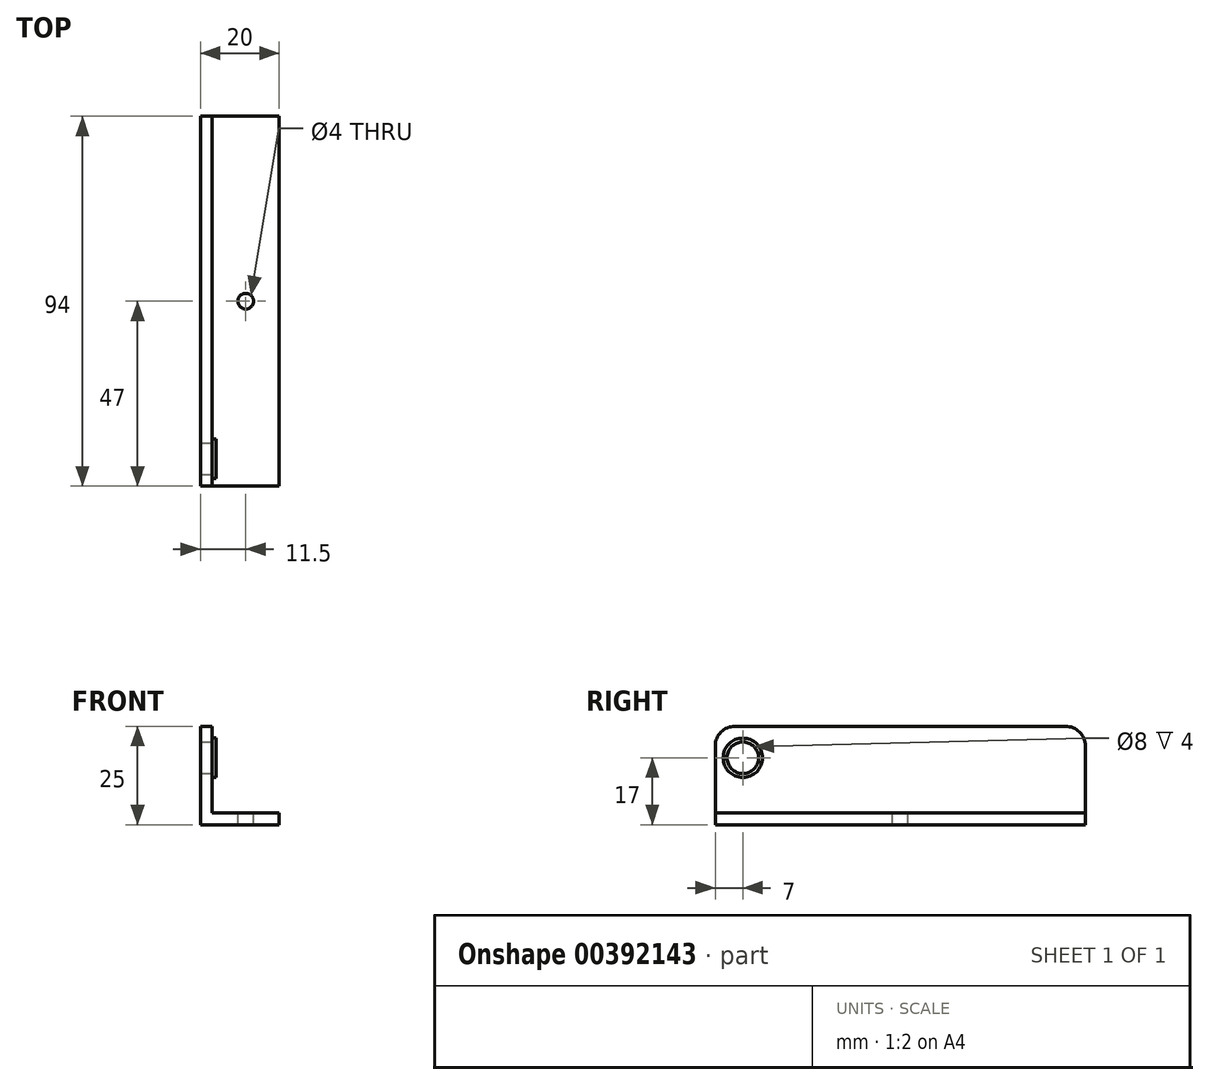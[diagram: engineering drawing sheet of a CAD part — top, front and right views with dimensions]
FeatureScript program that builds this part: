
annotation { "Feature Type Name" : "Feature", "Feature Type Description" : "" }
export const myFeature = defineFeature(function(context is Context, id is Id, definition is map)
    precondition{}
    {
        {
            var Q0;
            Q0=qCreatedBy(makeId("Top.planeOp"),FACE);
            var sketch = newSketch(context, id + "F0", { "sketchPlane" : qUnion([Q0])});
            skLineSegment(sketch, "E0.bottom", {"start": v(-65, 47) * mm, "end": v(-45, 47) * mm});
            skLineSegment(sketch, "E0.top", {"start": v(-65, -47) * mm, "end": v(-45, -47) * mm});
            skLineSegment(sketch, "E0.left", {"start": v(-65, 47) * mm, "end": v(-65, -47) * mm});
            skLineSegment(sketch, "E0.right", {"start": v(-45, 47) * mm, "end": v(-45, -47) * mm});
            skLineSegment(sketch, "E1", {"start": v(0, 47) * mm, "end": v(0, -47) * mm, "construction": true});
            skSolve(sketch);
        }
        {
            var Q0;
            Q0=makeQuery(id+"F0.imprint","IMPRINT",FACE,{"disambiguationData":[TD([[makeQuery(id+"F0.imprint","IMPRINT",EDGE,{"derivedFrom":sQuery(id+"F0.wireOp",EDGE,"E0.bottom")}),-1.0]])]});
            extrude(context, id + "F1", {"entities" : qUnion([Q0]), "depth" : 25 * mm});
        }
        {
            var Q0;
            Q0=makeQuery(id+"F1.opExtrude","SWEPT_FACE",FACE,{"disambiguationData":[OSD([sQuery(id+"F0.wireOp",EDGE,"E0.right")])]});
            var sketch = newSketch(context, id + "F2", { "sketchPlane" : qUnion([Q0])});
            skLineSegment(sketch, "E2.bottom", {"start": v(-47, 25) * mm, "end": v(47, 25) * mm});
            skLineSegment(sketch, "E2.top", {"start": v(-47, 3) * mm, "end": v(47, 3) * mm});
            skLineSegment(sketch, "E2.left", {"start": v(-47, 25) * mm, "end": v(-47, 3) * mm});
            skLineSegment(sketch, "E2.right", {"start": v(47, 25) * mm, "end": v(47, 3) * mm});
            skLineSegment(sketch, "E3", {"start": v(0, 0) * mm, "end": v(0, 25) * mm, "construction": true});
            skCircle(sketch, "E4", {"center": v(-40, 17) * mm, "radius": 11 * mm});
            skCircle(sketch, "E5", {"center": v(-40, 17) * mm, "radius": 13 * mm});
            skCircle(sketch, "E6", {"center": v(-40, 17) * mm, "radius": 4 * mm});
            skCircle(sketch, "E7", {"center": v(-40, 17) * mm, "radius": 5 * mm});
            skSolve(sketch);
        }
        {
            var Q0;
            {var subQ1=sQuery(id+"F2.wireOp",EDGE,"E2.bottom");Q0=makeQuery(id+"F2.imprint","IMPRINT",FACE,{"disambiguationData":[TD([[makeQuery(id+"F2.imprint","IMPRINT",EDGE,{"derivedFrom":subQ1}),1.0]])]});}
            var Q1;
            {var subQ0=sQuery(id+"F2.wireOp",EDGE,"E5");var subQ1=sQuery(id+"F2.wireOp",EDGE,"E2.left");var subQ2=makeQuery(id+"F2.imprint","INTERSECT",VERTEX,{"disambiguationData":[OD(0.0)],"derivedFrom":[subQ1,subQ0]});Q1=makeQuery(id+"F2.imprint","IMPRINT",FACE,{"disambiguationData":[TD([[makeQuery(id+"F2.imprint","IMPRINT",EDGE,{"disambiguationData":[TD([[subQ2,-1.0]])],"derivedFrom":subQ1}),1.0]])]});}
            var Q2;
            Q2=makeQuery(id+"F2.imprint","IMPRINT",FACE,{"disambiguationData":[TD([[makeQuery(id+"F2.imprint","IMPRINT",EDGE,{"derivedFrom":sQuery(id+"F2.wireOp",EDGE,"E7")}),-1.0]])]});
            var Q3;
            Q3=makeQuery(id+"F2.imprint","IMPRINT",FACE,{"disambiguationData":[TD([[makeQuery(id+"F2.imprint","IMPRINT",EDGE,{"derivedFrom":sQuery(id+"F2.wireOp",EDGE,"E6")}),-1.0]])]});
            extrude(context, id + "F3", {"entities" : qUnion([Q0, Q1, Q2, Q3]), "operationType" : NewBodyOperationType.REMOVE, "oppositeDirection" : true, "depth" : 17 * mm});
        }
        {
            var Q0;
            Q0=makeQuery(id+"F2.imprint","IMPRINT",FACE,{"disambiguationData":[TD([[makeQuery(id+"F2.imprint","IMPRINT",EDGE,{"derivedFrom":sQuery(id+"F2.wireOp",EDGE,"E6")}),1.0]])]});
            var Q1;
            Q1=makeQuery(id+"F1.opExtrude","SWEPT_FACE",FACE,{"disambiguationData":[OSD([sQuery(id+"F0.wireOp",EDGE,"E0.left")])]});
            extrude(context, id + "F4", {"entities" : qUnion([Q0]), "operationType" : NewBodyOperationType.REMOVE, "endBound" : BoundingType.UP_TO_SURFACE, "oppositeDirection" : true, "endBoundEntityFace" : qUnion([Q1]), "depth" : 25 * mm});
        }
        {
            var Q0;
            Q0=makeQuery(id+"F2.imprint","IMPRINT",FACE,{"disambiguationData":[TD([[makeQuery(id+"F2.imprint","IMPRINT",EDGE,{"derivedFrom":sQuery(id+"F2.wireOp",EDGE,"E6")}),-1.0]])]});
            extrude(context, id + "F5", {"entities" : qUnion([Q0]), "operationType" : NewBodyOperationType.ADD, "oppositeDirection" : true, "depth" : 17 * mm, "hasSecondDirection" : true, "secondDirectionOppositeDirection" : true, "secondDirectionDepth" : 16 * mm});
        }
        {
            var Q0;
            Q0=makeQuery(id+"F1.opExtrude","CAP_EDGE",EDGE,{"disambiguationData":[OSD([sQuery(id+"F0.wireOp",EDGE,"E0.top")])],"isStart":false});
            var Q1;
            Q1=makeQuery(id+"F1.opExtrude","CAP_EDGE",EDGE,{"disambiguationData":[OSD([sQuery(id+"F0.wireOp",EDGE,"E0.bottom")])],"isStart":false});
            fillet(context, id + "F6", {"entities" : qUnion([Q0, Q1]), "radius" : 5 * mm, "tangentPropagation" : true, "allowEdgeOverflow" : false});
        }
        {
            var Q0;
            Q0=makeQuery(id+"F3.boolean.opBoolean","COPY",FACE,{"derivedFrom":makeQuery(id+"F3.opExtrude","SWEPT_FACE",FACE,{"disambiguationData":[OSD([sQuery(id+"F2.wireOp",EDGE,"E2.top")])]})});
            var sketch = newSketch(context, id + "F7", { "sketchPlane" : qUnion([Q0])});
            skCircle(sketch, "E8", {"center": v(-53.5, 0) * mm, "radius": 2 * mm});
            skLineSegment(sketch, "E9", {"start": v(-62, 0) * mm, "end": v(-45, 0) * mm, "construction": true});
            skPoint(sketch, "E9.startSnap0", {"position": v(-62, 0) * mm});
            skPoint(sketch, "E9.endSnap0", {"position": v(-62, 0) * mm});
            skSolve(sketch);
        }
        {
            var Q0;
            Q0 = qSketchRegion(id + "F7", true);
            var Q1;
            Q1=makeQuery(id+"F1.opExtrude","CAP_FACE",FACE,{"disambiguationData":[OSD([sQuery(id+"F0.wireOp",EDGE,"E0.bottom"),sQuery(id+"F0.wireOp",EDGE,"E0.top"),sQuery(id+"F0.wireOp",EDGE,"E0.left"),sQuery(id+"F0.wireOp",EDGE,"E0.right")])],"isStart":true});
            extrude(context, id + "F8", {"entities" : qUnion([Q0]), "operationType" : NewBodyOperationType.REMOVE, "endBound" : BoundingType.UP_TO_SURFACE, "oppositeDirection" : true, "endBoundEntityFace" : qUnion([Q1]), "depth" : 25 * mm});
        }
    });
